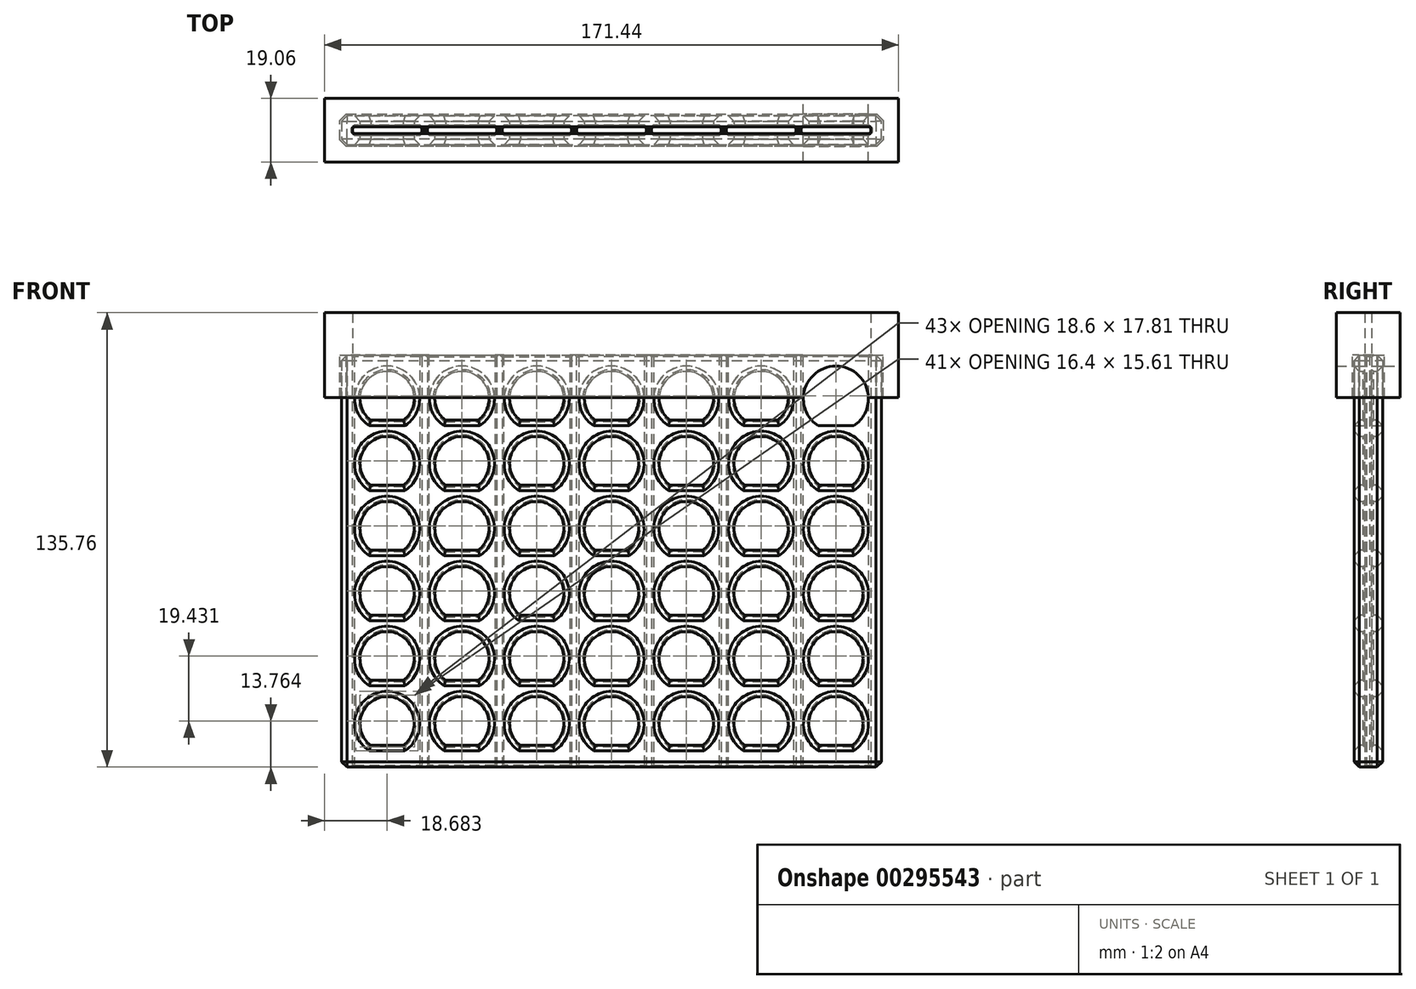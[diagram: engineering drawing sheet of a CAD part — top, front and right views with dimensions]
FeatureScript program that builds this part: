
annotation { "Feature Type Name" : "Feature", "Feature Type Description" : "" }
export const myFeature = defineFeature(function(context is Context, id is Id, definition is map)
    precondition{}
    {
        {
            var Q0;
            Q0=qCreatedBy(makeId("Top.planeOp"),FACE);
            var sketch = newSketch(context, id + "F0", { "sketchPlane" : qUnion([Q0])});
            skLineSegment(sketch, "E0.bottom", {"start": v(-75.88, 1.02) * mm, "end": v(-55.56, 1.02) * mm});
            skLineSegment(sketch, "E0.top", {"start": v(-75.88, -1.02) * mm, "end": v(-55.56, -1.02) * mm});
            skLineSegment(sketch, "E0.left", {"start": v(-75.88, 1.02) * mm, "end": v(-75.88, -1.02) * mm});
            skLineSegment(sketch, "E1.0", {"start": v(-79.06, 4.2) * mm, "end": v(0, 4.2) * mm});
            skLineSegment(sketch, "E1.1", {"start": v(-79.06, 4.2) * mm, "end": v(-79.06, -4.2) * mm});
            skLineSegment(sketch, "E1.2", {"start": v(-79.06, -4.2) * mm, "end": v(0, -4.2) * mm});
            skPoint(sketch, "E2.0", {"position": v(0, 0) * mm});
            skLineSegment(sketch, "E3", {"start": v(-10.16, 1.02) * mm, "end": v(-10.16, -1.02) * mm});
            skLineSegment(sketch, "E4.0", {"start": v(-11.75, 1.02) * mm, "end": v(-11.75, -1.02) * mm});
            skLineSegment(sketch, "E5", {"start": v(-32.07, 1.02) * mm, "end": v(-32.07, -1.02) * mm});
            skLineSegment(sketch, "E6", {"start": v(-33.66, 1.02) * mm, "end": v(-33.66, -1.02) * mm});
            skLineSegment(sketch, "E7", {"start": v(-53.98, 1.02) * mm, "end": v(-53.98, -1.02) * mm});
            skLineSegment(sketch, "E8", {"start": v(-55.56, 1.02) * mm, "end": v(-55.56, -1.02) * mm});
            skLineSegment(sketch, "E9", {"start": v(0, -4.2) * mm, "end": v(0, 4.2) * mm, "construction": true});
            skLineSegment(sketch, "E10.trimOffspring", {"start": v(-10.16, 1.02) * mm, "end": v(0, 1.02) * mm});
            skLineSegment(sketch, "E11.trimOffspring", {"start": v(-10.16, -1.02) * mm, "end": v(0, -1.02) * mm});
            skLineSegment(sketch, "E12.trimOffspring", {"start": v(-32.07, -1.02) * mm, "end": v(-11.75, -1.02) * mm});
            skLineSegment(sketch, "E13.trimOffspring", {"start": v(-32.07, 1.02) * mm, "end": v(-11.75, 1.02) * mm});
            skLineSegment(sketch, "E14.trimOffspring", {"start": v(-53.98, -1.02) * mm, "end": v(-33.66, -1.02) * mm});
            skLineSegment(sketch, "E15.trimOffspring", {"start": v(-53.98, 1.02) * mm, "end": v(-33.66, 1.02) * mm});
            skLineSegment(sketch, "E16.MirrorCS", {"start": v(79.06, 4.2) * mm, "end": v(0, 4.2) * mm});
            skLineSegment(sketch, "E17.MirrorCS", {"start": v(79.06, -4.2) * mm, "end": v(0, -4.2) * mm});
            skLineSegment(sketch, "E18.MirrorCS", {"start": v(10.16, -1.02) * mm, "end": v(0, -1.02) * mm});
            skLineSegment(sketch, "E19.MirrorCS", {"start": v(10.16, 1.02) * mm, "end": v(0, 1.02) * mm});
            skLineSegment(sketch, "E20.MirrorCS", {"start": v(10.16, 1.02) * mm, "end": v(10.16, -1.02) * mm});
            skLineSegment(sketch, "E21.MirrorCS", {"start": v(32.07, 1.02) * mm, "end": v(11.75, 1.02) * mm});
            skLineSegment(sketch, "E22.MirrorCS", {"start": v(11.75, 1.02) * mm, "end": v(11.75, -1.02) * mm});
            skLineSegment(sketch, "E23.MirrorCS", {"start": v(32.07, -1.02) * mm, "end": v(11.75, -1.02) * mm});
            skLineSegment(sketch, "E24.MirrorCS", {"start": v(32.07, 1.02) * mm, "end": v(32.07, -1.02) * mm});
            skLineSegment(sketch, "E25.MirrorCS", {"start": v(53.98, 1.02) * mm, "end": v(33.66, 1.02) * mm});
            skLineSegment(sketch, "E26.MirrorCS", {"start": v(33.66, 1.02) * mm, "end": v(33.66, -1.02) * mm});
            skLineSegment(sketch, "E27.MirrorCS", {"start": v(53.98, -1.02) * mm, "end": v(33.66, -1.02) * mm});
            skLineSegment(sketch, "E28.MirrorCS", {"start": v(53.98, 1.02) * mm, "end": v(53.98, -1.02) * mm});
            skLineSegment(sketch, "E29.MirrorCS", {"start": v(55.56, 1.02) * mm, "end": v(55.56, -1.02) * mm});
            skLineSegment(sketch, "E30.MirrorCS", {"start": v(75.88, 1.02) * mm, "end": v(55.56, 1.02) * mm});
            skLineSegment(sketch, "E31.MirrorCS", {"start": v(75.88, -1.02) * mm, "end": v(55.56, -1.02) * mm});
            skLineSegment(sketch, "E32.MirrorCS", {"start": v(75.88, 1.02) * mm, "end": v(75.88, -1.02) * mm});
            skLineSegment(sketch, "E33.MirrorCS", {"start": v(-158.12, -4.2) * mm, "end": v(-158.12, 4.2) * mm, "construction": true});
            skLineSegment(sketch, "E34.MirrorCS", {"start": v(79.06, 4.2) * mm, "end": v(79.06, -4.2) * mm});
            skSolve(sketch);
        }
        {
            var Q0;
            Q0 = qSketchRegion(id + "F0", true);
            extrude(context, id + "F1", {"entities" : qUnion([Q0]), "depth" : 120.65 * mm});
        }
        {
            var Q0;
            Q0=makeQuery(id+"F1.opExtrude","SWEPT_FACE",FACE,{"disambiguationData":[OSD([sQuery(id+"F0.wireOp",EDGE,"E1.2")])]});
            var sketch = newSketch(context, id + "F2", { "sketchPlane" : qUnion([Q0])});
            skArc(sketch, "E35.2.0.5", {"start": v(48.58, 6.35) * mm, "mid": v(43.82, 20.64) * mm, "end": v(39.05, 6.35) * mm});
            skArc(sketch, "E35.3.0.4", {"start": v(70.49, 25.4) * mm, "mid": v(65.72, 39.69) * mm, "end": v(60.96, 25.4) * mm});
            skArc(sketch, "E35.3.0.5", {"start": v(70.48, 6.35) * mm, "mid": v(65.72, 20.64) * mm, "end": v(60.96, 6.35) * mm});
            skLineSegment(sketch, "E36", {"start": v(65.72, 12.7) * mm, "end": v(65.72, -4.67) * mm, "construction": true});
            skPoint(sketch, "E37.orphan", {"position": v(83.09, -4.67) * mm});
            skLineSegment(sketch, "E38", {"start": v(70.48, 6.35) * mm, "end": v(60.96, 6.35) * mm});
            skLineSegment(sketch, "E39.trimOffspring", {"start": v(48.58, 6.35) * mm, "end": v(39.05, 6.35) * mm});
            skLineSegment(sketch, "E40.0.1.0", {"start": v(70.49, 25.4) * mm, "end": v(60.96, 25.4) * mm});
            skLineSegment(sketch, "E41.0.1.0", {"start": v(70.49, 44.45) * mm, "end": v(60.96, 44.45) * mm});
            skArc(sketch, "E41.0.1.1", {"start": v(70.49, 44.45) * mm, "mid": v(65.72, 58.74) * mm, "end": v(60.96, 44.45) * mm});
            skLineSegment(sketch, "E41.0.2.0", {"start": v(70.49, 63.5) * mm, "end": v(60.96, 63.5) * mm});
            skArc(sketch, "E41.0.2.1", {"start": v(70.49, 63.5) * mm, "mid": v(65.72, 77.79) * mm, "end": v(60.96, 63.5) * mm});
            skLineSegment(sketch, "E41.0.3.0", {"start": v(70.49, 82.55) * mm, "end": v(60.96, 82.55) * mm});
            skArc(sketch, "E41.0.3.1", {"start": v(70.49, 82.55) * mm, "mid": v(65.72, 96.84) * mm, "end": v(60.96, 82.55) * mm});
            skLineSegment(sketch, "E41.0.4.0", {"start": v(70.49, 101.6) * mm, "end": v(60.96, 101.6) * mm});
            skArc(sketch, "E41.0.4.1", {"start": v(70.49, 101.6) * mm, "mid": v(65.72, 115.89) * mm, "end": v(60.96, 101.6) * mm});
            skLineSegment(sketch, "E41.1.0.0", {"start": v(48.58, 25.4) * mm, "end": v(39.05, 25.4) * mm});
            skArc(sketch, "E41.1.0.1", {"start": v(48.58, 25.4) * mm, "mid": v(43.81, 39.69) * mm, "end": v(39.05, 25.4) * mm});
            skLineSegment(sketch, "E41.1.1.0", {"start": v(48.58, 44.45) * mm, "end": v(39.05, 44.45) * mm});
            skArc(sketch, "E41.1.1.1", {"start": v(48.58, 44.45) * mm, "mid": v(43.81, 58.74) * mm, "end": v(39.05, 44.45) * mm});
            skLineSegment(sketch, "E41.1.2.0", {"start": v(48.58, 63.5) * mm, "end": v(39.05, 63.5) * mm});
            skArc(sketch, "E41.1.2.1", {"start": v(48.58, 63.5) * mm, "mid": v(43.81, 77.79) * mm, "end": v(39.05, 63.5) * mm});
            skLineSegment(sketch, "E41.1.3.0", {"start": v(48.58, 82.55) * mm, "end": v(39.05, 82.55) * mm});
            skArc(sketch, "E41.1.3.1", {"start": v(48.58, 82.55) * mm, "mid": v(43.81, 96.84) * mm, "end": v(39.05, 82.55) * mm});
            skLineSegment(sketch, "E41.1.4.0", {"start": v(48.58, 101.6) * mm, "end": v(39.05, 101.6) * mm});
            skArc(sketch, "E41.1.4.1", {"start": v(48.58, 101.6) * mm, "mid": v(43.81, 115.89) * mm, "end": v(39.05, 101.6) * mm});
            skLineSegment(sketch, "E41.2.0.0", {"start": v(26.67, 25.4) * mm, "end": v(17.14, 25.4) * mm});
            skArc(sketch, "E41.2.0.1", {"start": v(26.67, 25.4) * mm, "mid": v(21.9, 39.69) * mm, "end": v(17.14, 25.4) * mm});
            skLineSegment(sketch, "E41.2.1.0", {"start": v(26.67, 44.45) * mm, "end": v(17.14, 44.45) * mm});
            skArc(sketch, "E41.2.1.1", {"start": v(26.67, 44.45) * mm, "mid": v(21.9, 58.74) * mm, "end": v(17.14, 44.45) * mm});
            skLineSegment(sketch, "E41.2.2.0", {"start": v(26.67, 63.5) * mm, "end": v(17.14, 63.5) * mm});
            skArc(sketch, "E41.2.2.1", {"start": v(26.67, 63.5) * mm, "mid": v(21.9, 77.79) * mm, "end": v(17.14, 63.5) * mm});
            skLineSegment(sketch, "E41.2.3.0", {"start": v(26.67, 82.55) * mm, "end": v(17.14, 82.55) * mm});
            skArc(sketch, "E41.2.3.1", {"start": v(26.67, 82.55) * mm, "mid": v(21.9, 96.84) * mm, "end": v(17.14, 82.55) * mm});
            skLineSegment(sketch, "E41.2.4.0", {"start": v(26.67, 101.6) * mm, "end": v(17.14, 101.6) * mm});
            skArc(sketch, "E41.2.4.1", {"start": v(26.67, 101.6) * mm, "mid": v(21.9, 115.89) * mm, "end": v(17.14, 101.6) * mm});
            skLineSegment(sketch, "E41.3.0.0", {"start": v(4.76, 25.4) * mm, "end": v(-4.76, 25.4) * mm});
            skArc(sketch, "E41.3.0.1", {"start": v(4.76, 25.4) * mm, "mid": v(0, 39.69) * mm, "end": v(-4.76, 25.4) * mm});
            skLineSegment(sketch, "E41.3.1.0", {"start": v(4.76, 44.45) * mm, "end": v(-4.76, 44.45) * mm});
            skArc(sketch, "E41.3.1.1", {"start": v(4.76, 44.45) * mm, "mid": v(0, 58.74) * mm, "end": v(-4.76, 44.45) * mm});
            skLineSegment(sketch, "E41.3.2.0", {"start": v(4.76, 63.5) * mm, "end": v(-4.76, 63.5) * mm});
            skArc(sketch, "E41.3.2.1", {"start": v(4.76, 63.5) * mm, "mid": v(0, 77.79) * mm, "end": v(-4.76, 63.5) * mm});
            skLineSegment(sketch, "E41.3.3.0", {"start": v(4.76, 82.55) * mm, "end": v(-4.76, 82.55) * mm});
            skArc(sketch, "E41.3.3.1", {"start": v(4.76, 82.55) * mm, "mid": v(0, 96.84) * mm, "end": v(-4.76, 82.55) * mm});
            skLineSegment(sketch, "E41.3.4.0", {"start": v(4.76, 101.6) * mm, "end": v(-4.76, 101.6) * mm});
            skArc(sketch, "E41.3.4.1", {"start": v(4.76, 101.6) * mm, "mid": v(0, 115.89) * mm, "end": v(-4.76, 101.6) * mm});
            skLineSegment(sketch, "E41.4.0.0", {"start": v(-17.15, 25.4) * mm, "end": v(-26.67, 25.4) * mm});
            skArc(sketch, "E41.4.0.1", {"start": v(-17.15, 25.4) * mm, "mid": v(-21.9, 39.69) * mm, "end": v(-26.67, 25.4) * mm});
            skLineSegment(sketch, "E41.4.1.0", {"start": v(-17.15, 44.45) * mm, "end": v(-26.67, 44.45) * mm});
            skArc(sketch, "E41.4.1.1", {"start": v(-17.15, 44.45) * mm, "mid": v(-21.9, 58.74) * mm, "end": v(-26.67, 44.45) * mm});
            skLineSegment(sketch, "E41.4.2.0", {"start": v(-17.15, 63.5) * mm, "end": v(-26.67, 63.5) * mm});
            skArc(sketch, "E41.4.2.1", {"start": v(-17.15, 63.5) * mm, "mid": v(-21.9, 77.79) * mm, "end": v(-26.67, 63.5) * mm});
            skLineSegment(sketch, "E41.4.3.0", {"start": v(-17.15, 82.55) * mm, "end": v(-26.67, 82.55) * mm});
            skArc(sketch, "E41.4.3.1", {"start": v(-17.15, 82.55) * mm, "mid": v(-21.9, 96.84) * mm, "end": v(-26.67, 82.55) * mm});
            skLineSegment(sketch, "E41.4.4.0", {"start": v(-17.15, 101.6) * mm, "end": v(-26.67, 101.6) * mm});
            skArc(sketch, "E41.4.4.1", {"start": v(-17.15, 101.6) * mm, "mid": v(-21.9, 115.89) * mm, "end": v(-26.67, 101.6) * mm});
            skLineSegment(sketch, "E41.5.0.0", {"start": v(-39.05, 25.4) * mm, "end": v(-48.58, 25.4) * mm});
            skArc(sketch, "E41.5.0.1", {"start": v(-39.05, 25.4) * mm, "mid": v(-43.82, 39.69) * mm, "end": v(-48.58, 25.4) * mm});
            skLineSegment(sketch, "E41.5.1.0", {"start": v(-39.05, 44.45) * mm, "end": v(-48.58, 44.45) * mm});
            skArc(sketch, "E41.5.1.1", {"start": v(-39.05, 44.45) * mm, "mid": v(-43.82, 58.74) * mm, "end": v(-48.58, 44.45) * mm});
            skLineSegment(sketch, "E41.5.2.0", {"start": v(-39.05, 63.5) * mm, "end": v(-48.58, 63.5) * mm});
            skArc(sketch, "E41.5.2.1", {"start": v(-39.05, 63.5) * mm, "mid": v(-43.82, 77.79) * mm, "end": v(-48.58, 63.5) * mm});
            skLineSegment(sketch, "E41.5.3.0", {"start": v(-39.05, 82.55) * mm, "end": v(-48.58, 82.55) * mm});
            skArc(sketch, "E41.5.3.1", {"start": v(-39.05, 82.55) * mm, "mid": v(-43.82, 96.84) * mm, "end": v(-48.58, 82.55) * mm});
            skLineSegment(sketch, "E41.5.4.0", {"start": v(-39.05, 101.6) * mm, "end": v(-48.58, 101.6) * mm});
            skArc(sketch, "E41.5.4.1", {"start": v(-39.05, 101.6) * mm, "mid": v(-43.82, 115.89) * mm, "end": v(-48.58, 101.6) * mm});
            skLineSegment(sketch, "E41.6.0.0", {"start": v(-60.96, 25.4) * mm, "end": v(-70.49, 25.4) * mm});
            skArc(sketch, "E41.6.0.1", {"start": v(-60.96, 25.4) * mm, "mid": v(-65.72, 39.69) * mm, "end": v(-70.49, 25.4) * mm});
            skLineSegment(sketch, "E41.6.1.0", {"start": v(-60.96, 44.45) * mm, "end": v(-70.49, 44.45) * mm});
            skArc(sketch, "E41.6.1.1", {"start": v(-60.96, 44.45) * mm, "mid": v(-65.72, 58.74) * mm, "end": v(-70.49, 44.45) * mm});
            skLineSegment(sketch, "E41.6.2.0", {"start": v(-60.96, 63.5) * mm, "end": v(-70.49, 63.5) * mm});
            skArc(sketch, "E41.6.2.1", {"start": v(-60.96, 63.5) * mm, "mid": v(-65.72, 77.79) * mm, "end": v(-70.49, 63.5) * mm});
            skLineSegment(sketch, "E41.6.3.0", {"start": v(-60.96, 82.55) * mm, "end": v(-70.49, 82.55) * mm});
            skArc(sketch, "E41.6.3.1", {"start": v(-60.96, 82.55) * mm, "mid": v(-65.72, 96.84) * mm, "end": v(-70.49, 82.55) * mm});
            skLineSegment(sketch, "E41.6.4.0", {"start": v(-60.96, 101.6) * mm, "end": v(-70.49, 101.6) * mm});
            skArc(sketch, "E41.6.4.1", {"start": v(-60.96, 101.6) * mm, "mid": v(-65.72, 115.89) * mm, "end": v(-70.49, 101.6) * mm});
            skLineSegment(sketch, "E41.direction1", {"start": v(60.96, 25.4) * mm, "end": v(39.05, 25.4) * mm, "construction": true});
            skLineSegment(sketch, "E41.direction2", {"start": v(60.96, 25.4) * mm, "end": v(60.96, 44.45) * mm, "construction": true});
            skLineSegment(sketch, "E42.1.0.0", {"start": v(26.67, 6.35) * mm, "end": v(17.14, 6.35) * mm});
            skArc(sketch, "E42.1.0.1", {"start": v(26.67, 6.35) * mm, "mid": v(21.9, 20.64) * mm, "end": v(17.14, 6.35) * mm});
            skLineSegment(sketch, "E42.2.0.0", {"start": v(4.76, 6.35) * mm, "end": v(-4.76, 6.35) * mm});
            skArc(sketch, "E42.2.0.1", {"start": v(4.76, 6.35) * mm, "mid": v(0, 20.64) * mm, "end": v(-4.76, 6.35) * mm});
            skLineSegment(sketch, "E42.3.0.0", {"start": v(-17.15, 6.35) * mm, "end": v(-26.67, 6.35) * mm});
            skArc(sketch, "E42.3.0.1", {"start": v(-17.15, 6.35) * mm, "mid": v(-21.9, 20.64) * mm, "end": v(-26.67, 6.35) * mm});
            skLineSegment(sketch, "E42.4.0.0", {"start": v(-39.05, 6.35) * mm, "end": v(-48.58, 6.35) * mm});
            skArc(sketch, "E42.4.0.1", {"start": v(-39.05, 6.35) * mm, "mid": v(-43.82, 20.64) * mm, "end": v(-48.58, 6.35) * mm});
            skLineSegment(sketch, "E42.5.0.0", {"start": v(-60.96, 6.35) * mm, "end": v(-70.49, 6.35) * mm});
            skArc(sketch, "E42.5.0.1", {"start": v(-60.96, 6.35) * mm, "mid": v(-65.72, 20.64) * mm, "end": v(-70.49, 6.35) * mm});
            skLineSegment(sketch, "E42.direction1", {"start": v(39.05, 6.35) * mm, "end": v(17.14, 6.35) * mm, "construction": true});
            skSolve(sketch);
        }
        {
            var Q0;
            Q0 = qSketchRegion(id + "F2", true);
            extrude(context, id + "F3", {"entities" : qUnion([Q0]), "operationType" : NewBodyOperationType.REMOVE, "oppositeDirection" : true, "depth" : 25.4 * mm});
        }
        {
            var Q0;
            Q0=makeQuery(id+"F1.opExtrude","SWEPT_FACE",FACE,{"disambiguationData":[OSD([sQuery(id+"F0.wireOp",EDGE,"E0.bottom")])]});
            var Q1;
            Q1=makeQuery(id+"F1.opExtrude","SWEPT_FACE",FACE,{"disambiguationData":[OSD([sQuery(id+"F0.wireOp",EDGE,"E15.trimOffspring")])]});
            var Q2;
            Q2=makeQuery(id+"F1.opExtrude","SWEPT_FACE",FACE,{"disambiguationData":[OSD([sQuery(id+"F0.wireOp",EDGE,"E13.trimOffspring")])]});
            var Q3;
            Q3=makeQuery(id+"F1.opExtrude","SWEPT_FACE",FACE,{"disambiguationData":[OSD([sQuery(id+"F0.wireOp",EDGE,"E10.trimOffspring"),sQuery(id+"F0.wireOp",EDGE,"E19.MirrorCS")])]});
            var Q4;
            Q4=makeQuery(id+"F1.opExtrude","SWEPT_FACE",FACE,{"disambiguationData":[OSD([sQuery(id+"F0.wireOp",EDGE,"E21.MirrorCS")])]});
            var Q5;
            Q5=makeQuery(id+"F1.opExtrude","SWEPT_FACE",FACE,{"disambiguationData":[OSD([sQuery(id+"F0.wireOp",EDGE,"E25.MirrorCS")])]});
            var Q6;
            Q6=makeQuery(id+"F1.opExtrude","SWEPT_FACE",FACE,{"disambiguationData":[OSD([sQuery(id+"F0.wireOp",EDGE,"E30.MirrorCS")])]});
            var Q7;
            Q7=makeQuery(id+"F1.opExtrude","SWEPT_FACE",FACE,{"disambiguationData":[OSD([sQuery(id+"F0.wireOp",EDGE,"E31.MirrorCS")])]});
            var Q8;
            Q8=makeQuery(id+"F1.opExtrude","SWEPT_FACE",FACE,{"disambiguationData":[OSD([sQuery(id+"F0.wireOp",EDGE,"E27.MirrorCS")])]});
            var Q9;
            Q9=makeQuery(id+"F1.opExtrude","SWEPT_FACE",FACE,{"disambiguationData":[OSD([sQuery(id+"F0.wireOp",EDGE,"E23.MirrorCS")])]});
            var Q10;
            Q10=makeQuery(id+"F1.opExtrude","SWEPT_FACE",FACE,{"disambiguationData":[OSD([sQuery(id+"F0.wireOp",EDGE,"E11.trimOffspring"),sQuery(id+"F0.wireOp",EDGE,"E18.MirrorCS")])]});
            var Q11;
            Q11=makeQuery(id+"F1.opExtrude","SWEPT_FACE",FACE,{"disambiguationData":[OSD([sQuery(id+"F0.wireOp",EDGE,"E12.trimOffspring")])]});
            var Q12;
            Q12=makeQuery(id+"F1.opExtrude","SWEPT_FACE",FACE,{"disambiguationData":[OSD([sQuery(id+"F0.wireOp",EDGE,"E0.top")])]});
            var Q13;
            Q13=makeQuery(id+"F1.opExtrude","SWEPT_FACE",FACE,{"disambiguationData":[OSD([sQuery(id+"F0.wireOp",EDGE,"E14.trimOffspring")])]});
            chamfer(context, id + "F4", {"entities" : qUnion([Q0, Q1, Q2, Q3, Q4, Q5, Q6, Q7, Q8, Q9, Q10, Q11, Q12, Q13]), "width" : 0.5 * mm, "tangentPropagation" : true});
        }
        {
            var Q0;
            Q0=makeQuery(id+"F1.opExtrude","SWEPT_FACE",FACE,{"disambiguationData":[OSD([sQuery(id+"F0.wireOp",EDGE,"E1.0"),sQuery(id+"F0.wireOp",EDGE,"E16.MirrorCS")])]});
            var Q1;
            Q1=makeQuery(id+"F1.opExtrude","SWEPT_FACE",FACE,{"disambiguationData":[OSD([sQuery(id+"F0.wireOp",EDGE,"E1.2"),sQuery(id+"F0.wireOp",EDGE,"E17.MirrorCS")])]});
            var Q2;
            Q2=makeQuery(id+"F1.opExtrude","CAP_EDGE",EDGE,{"disambiguationData":[OSD([sQuery(id+"F0.wireOp",EDGE,"E34.MirrorCS")])],"isStart":false});
            var Q3;
            Q3=makeQuery(id+"F1.opExtrude","CAP_EDGE",EDGE,{"disambiguationData":[OSD([sQuery(id+"F0.wireOp",EDGE,"E1.1")])],"isStart":false});
            var Q4;
            Q4=makeQuery(id+"F1.opExtrude","CAP_EDGE",EDGE,{"disambiguationData":[OSD([sQuery(id+"F0.wireOp",EDGE,"E1.1")])],"isStart":true});
            var Q5;
            Q5=makeQuery(id+"F1.opExtrude","CAP_EDGE",EDGE,{"disambiguationData":[OSD([sQuery(id+"F0.wireOp",EDGE,"E34.MirrorCS")])],"isStart":true});
            chamfer(context, id + "F5", {"entities" : qUnion([Q0, Q1, Q2, Q3, Q4, Q5]), "width" : 1.59 * mm, "tangentPropagation" : true});
        }
        {
            var Q0;
            Q0=makeQuery(id+"F1.opExtrude","SWEPT_BODY",BODY,{"disambiguationData":[OSD([sQuery(id+"F0.wireOp",EDGE,"E0.bottom"),sQuery(id+"F0.wireOp",EDGE,"E0.top"),sQuery(id+"F0.wireOp",EDGE,"E0.left"),sQuery(id+"F0.wireOp",EDGE,"E1.0"),sQuery(id+"F0.wireOp",EDGE,"E1.1"),sQuery(id+"F0.wireOp",EDGE,"E1.2"),sQuery(id+"F0.wireOp",EDGE,"E3"),sQuery(id+"F0.wireOp",EDGE,"E4.0"),sQuery(id+"F0.wireOp",EDGE,"E5"),sQuery(id+"F0.wireOp",EDGE,"E6"),sQuery(id+"F0.wireOp",EDGE,"E7"),sQuery(id+"F0.wireOp",EDGE,"E8"),sQuery(id+"F0.wireOp",EDGE,"E10.trimOffspring"),sQuery(id+"F0.wireOp",EDGE,"E11.trimOffspring"),sQuery(id+"F0.wireOp",EDGE,"E12.trimOffspring"),sQuery(id+"F0.wireOp",EDGE,"E13.trimOffspring"),sQuery(id+"F0.wireOp",EDGE,"E14.trimOffspring"),sQuery(id+"F0.wireOp",EDGE,"E15.trimOffspring"),sQuery(id+"F0.wireOp",EDGE,"E16.MirrorCS"),sQuery(id+"F0.wireOp",EDGE,"E17.MirrorCS"),sQuery(id+"F0.wireOp",EDGE,"E18.MirrorCS"),sQuery(id+"F0.wireOp",EDGE,"E19.MirrorCS"),sQuery(id+"F0.wireOp",EDGE,"E20.MirrorCS"),sQuery(id+"F0.wireOp",EDGE,"E21.MirrorCS"),sQuery(id+"F0.wireOp",EDGE,"E22.MirrorCS"),sQuery(id+"F0.wireOp",EDGE,"E23.MirrorCS"),sQuery(id+"F0.wireOp",EDGE,"E24.MirrorCS"),sQuery(id+"F0.wireOp",EDGE,"E25.MirrorCS"),sQuery(id+"F0.wireOp",EDGE,"E26.MirrorCS"),sQuery(id+"F0.wireOp",EDGE,"E27.MirrorCS"),sQuery(id+"F0.wireOp",EDGE,"E28.MirrorCS"),sQuery(id+"F0.wireOp",EDGE,"E29.MirrorCS"),sQuery(id+"F0.wireOp",EDGE,"E30.MirrorCS"),sQuery(id+"F0.wireOp",EDGE,"E31.MirrorCS"),sQuery(id+"F0.wireOp",EDGE,"E32.MirrorCS"),sQuery(id+"F0.wireOp",EDGE,"E34.MirrorCS")])]});
            var Q1;
            Q1=qCreatedBy(makeId("Origin.pointOp"),VERTEX);
            transform(context, id + "F6", {"entities" : qUnion([Q0]), "transformType" : TransformType.SCALE_UNIFORMLY, "scale" : 1.02, "scalePoint" : qUnion([Q1]), "makeCopy" : false});
        }
        {
            var Q0;
            Q0=makeQuery(id+"F1.opExtrude","CAP_FACE",FACE,{"disambiguationData":[OSD([sQuery(id+"F0.wireOp",EDGE,"E0.bottom"),sQuery(id+"F0.wireOp",EDGE,"E0.top"),sQuery(id+"F0.wireOp",EDGE,"E0.left"),sQuery(id+"F0.wireOp",EDGE,"E1.0"),sQuery(id+"F0.wireOp",EDGE,"E1.1"),sQuery(id+"F0.wireOp",EDGE,"E1.2"),sQuery(id+"F0.wireOp",EDGE,"E3"),sQuery(id+"F0.wireOp",EDGE,"E4.0"),sQuery(id+"F0.wireOp",EDGE,"E5"),sQuery(id+"F0.wireOp",EDGE,"E6"),sQuery(id+"F0.wireOp",EDGE,"E7"),sQuery(id+"F0.wireOp",EDGE,"E8"),sQuery(id+"F0.wireOp",EDGE,"E10.trimOffspring"),sQuery(id+"F0.wireOp",EDGE,"E11.trimOffspring"),sQuery(id+"F0.wireOp",EDGE,"E12.trimOffspring"),sQuery(id+"F0.wireOp",EDGE,"E13.trimOffspring"),sQuery(id+"F0.wireOp",EDGE,"E14.trimOffspring"),sQuery(id+"F0.wireOp",EDGE,"E15.trimOffspring"),sQuery(id+"F0.wireOp",EDGE,"E16.MirrorCS"),sQuery(id+"F0.wireOp",EDGE,"E17.MirrorCS"),sQuery(id+"F0.wireOp",EDGE,"E18.MirrorCS"),sQuery(id+"F0.wireOp",EDGE,"E19.MirrorCS"),sQuery(id+"F0.wireOp",EDGE,"E20.MirrorCS"),sQuery(id+"F0.wireOp",EDGE,"E21.MirrorCS"),sQuery(id+"F0.wireOp",EDGE,"E22.MirrorCS"),sQuery(id+"F0.wireOp",EDGE,"E23.MirrorCS"),sQuery(id+"F0.wireOp",EDGE,"E24.MirrorCS"),sQuery(id+"F0.wireOp",EDGE,"E25.MirrorCS"),sQuery(id+"F0.wireOp",EDGE,"E26.MirrorCS"),sQuery(id+"F0.wireOp",EDGE,"E27.MirrorCS"),sQuery(id+"F0.wireOp",EDGE,"E28.MirrorCS"),sQuery(id+"F0.wireOp",EDGE,"E29.MirrorCS"),sQuery(id+"F0.wireOp",EDGE,"E30.MirrorCS"),sQuery(id+"F0.wireOp",EDGE,"E31.MirrorCS"),sQuery(id+"F0.wireOp",EDGE,"E32.MirrorCS"),sQuery(id+"F0.wireOp",EDGE,"E34.MirrorCS")])],"isStart":false});
            var sketch = newSketch(context, id + "F7", { "sketchPlane" : qUnion([Q0])});
            skLineSegment(sketch, "E43.0", {"start": v(-81.15, 2.87) * mm, "end": v(-79.23, 4.78) * mm});
            skLineSegment(sketch, "E43.1", {"start": v(-81.15, -2.87) * mm, "end": v(-81.15, 2.87) * mm});
            skLineSegment(sketch, "E43.2", {"start": v(-79.23, 4.78) * mm, "end": v(79.23, 4.78) * mm});
            skLineSegment(sketch, "E43.3", {"start": v(-79.23, -4.78) * mm, "end": v(-81.15, -2.87) * mm});
            skLineSegment(sketch, "E43.4", {"start": v(79.23, 4.78) * mm, "end": v(81.15, 2.87) * mm});
            skLineSegment(sketch, "E43.5", {"start": v(81.15, 2.87) * mm, "end": v(81.15, -2.87) * mm});
            skLineSegment(sketch, "E43.6", {"start": v(81.15, -2.87) * mm, "end": v(79.23, -4.78) * mm});
            skLineSegment(sketch, "E43.7", {"start": v(79.23, -4.78) * mm, "end": v(-79.23, -4.78) * mm});
            skLineSegment(sketch, "E44.bottom", {"start": v(-85.73, -9.53) * mm, "end": v(85.73, -9.53) * mm});
            skLineSegment(sketch, "E44.top", {"start": v(-85.73, 9.53) * mm, "end": v(85.73, 9.53) * mm});
            skLineSegment(sketch, "E44.left", {"start": v(-85.73, -9.53) * mm, "end": v(-85.73, 9.53) * mm});
            skLineSegment(sketch, "E44.right", {"start": v(85.73, -9.53) * mm, "end": v(85.73, 9.53) * mm});
            skPoint(sketch, "E44.middle", {"position": v(0, 0) * mm});
            skSolve(sketch);
        }
        {
            var Q0;
            Q0 = qSketchRegion(id + "F7", true);
            extrude(context, id + "F8", {"entities" : qUnion([Q0]), "oppositeDirection" : true, "depth" : 12.7 * mm});
        }
        {
            var Q0;
            Q0=makeQuery(id+"F8.opExtrude","SWEPT_FACE",FACE,{"disambiguationData":[OSD([sQuery(id+"F7.wireOp",EDGE,"E44.top")])]});
            var sketch = newSketch(context, id + "F9", { "sketchPlane" : qUnion([Q0])});
            skArc(sketch, "E45.0", {"start": v(-72.4, 102.01) * mm, "mid": v(-67.04, 119.82) * mm, "end": v(-61.67, 102.01) * mm});
            skLineSegment(sketch, "E46.0", {"start": v(-61.67, 102.01) * mm, "end": v(-72.4, 102.01) * mm});
            skSolve(sketch);
        }
        {
            var Q0;
            Q0 = qSketchRegion(id + "F9", true);
            extrude(context, id + "F10", {"entities" : qUnion([Q0]), "operationType" : NewBodyOperationType.REMOVE, "endBound" : BoundingType.THROUGH_ALL, "oppositeDirection" : true, "depth" : 25.4 * mm});
        }
        {
            var Q0;
            Q0=makeQuery(id+"F8.opExtrude","CAP_FACE",FACE,{"disambiguationData":[OSD([sQuery(id+"F7.wireOp",EDGE,"E43.0"),sQuery(id+"F7.wireOp",EDGE,"E43.1"),sQuery(id+"F7.wireOp",EDGE,"E43.2"),sQuery(id+"F7.wireOp",EDGE,"E43.3"),sQuery(id+"F7.wireOp",EDGE,"E43.4"),sQuery(id+"F7.wireOp",EDGE,"E43.5"),sQuery(id+"F7.wireOp",EDGE,"E43.6"),sQuery(id+"F7.wireOp",EDGE,"E43.7"),sQuery(id+"F7.wireOp",EDGE,"E44.bottom"),sQuery(id+"F7.wireOp",EDGE,"E44.top"),sQuery(id+"F7.wireOp",EDGE,"E44.left"),sQuery(id+"F7.wireOp",EDGE,"E44.right")])],"isStart":true});
            var sketch = newSketch(context, id + "F11", { "sketchPlane" : qUnion([Q0])});
            skLineSegment(sketch, "E47.0", {"start": v(-77.4, -1.04) * mm, "end": v(77.4, -1.04) * mm});
            skLineSegment(sketch, "E48.0", {"start": v(77.4, 1.04) * mm, "end": v(-77.4, 1.04) * mm});
            skLineSegment(sketch, "E49.0", {"start": v(-85.73, -9.53) * mm, "end": v(85.73, -9.53) * mm});
            skLineSegment(sketch, "E50.0", {"start": v(-85.73, 9.53) * mm, "end": v(85.73, 9.53) * mm});
            skLineSegment(sketch, "E51.0", {"start": v(77.4, -1.04) * mm, "end": v(77.4, 1.04) * mm});
            skPoint(sketch, "E52.orphan", {"position": v(76.88, 1.04) * mm});
            skPoint(sketch, "E53.orphan", {"position": v(77.4, -0.52) * mm});
            skPoint(sketch, "E54.orphan", {"position": v(76.88, -1.04) * mm});
            skPoint(sketch, "E55.orphan", {"position": v(77.4, 0.52) * mm});
            skLineSegment(sketch, "E56.0", {"start": v(-85.73, -9.53) * mm, "end": v(-85.73, 9.53) * mm});
            skLineSegment(sketch, "E57.0", {"start": v(-77.4, 1.04) * mm, "end": v(-77.4, -1.04) * mm});
            skPoint(sketch, "E58.orphan", {"position": v(57.2, 1.04) * mm});
            skPoint(sketch, "E59.orphan", {"position": v(-77.4, 0.52) * mm});
            skPoint(sketch, "E60.orphan", {"position": v(57.2, -1.04) * mm});
            skPoint(sketch, "E61.orphan", {"position": v(-77.4, -0.52) * mm});
            skLineSegment(sketch, "E62", {"start": v(85.73, 9.53) * mm, "end": v(85.73, -9.53) * mm});
            skSolve(sketch);
        }
        {
            var Q0;
            Q0 = qSketchRegion(id + "F11", true);
            extrude(context, id + "F12", {"entities" : qUnion([Q0]), "operationType" : NewBodyOperationType.ADD, "depth" : 12.7 * mm});
        }
    });
